# Revit family: IS_ConnectFreedom_E5485_BIM_DE
name_source: partatom
category: Plumbing Fixtures
revit_build: Autodesk Revit MEP 2015 (Build: 20140606_1530(x64)
units: mm (PartAtom-declared; Revit-internal decimal feet)

## types (1)
- E548501 - CONNECT FREEDOM - Basin 60X55 White
    BIMobject category = Basins
    BOSUseNativeGeometries = 1
    Brand url = http://www.idealstandard.co.uk
    Description = E548501 CONNECT FREEDOM accessible washbasin 600x555mm, 1 taphole, no overflow
    DrainSize = 42 mm  [stored 0.137795 ft]
    EAN code = https://5017830470328
    Edition number = 1
    IfcExportAs = WASHHANDBASIN
    IfcExportType = WASHBASIN
    Installation instructions = http://www.idealspec.co.uk
    Manufacturer name = Ideal Standard
    ManufacturerURL = www.idealstandard.com
    Material = Vitreous china
    Material main = Ceramics
    Model = E548501
    ModelNumber = E548501
    Name = CONNECT FREEDOM accessible washbasin 600x555mm, 1 taphole, no overflow
    NettWeight = 17.5 kg
    Nominal height = 165
    Nominal width = 600
    NominalDepth = 0 mm  [stored 0 ft]
    NominalHeight = 165 mm  [stored 0.541339 ft]
    NominalLength = 555 mm  [stored 1.82087 ft]
    NominalWidth = 600 mm  [stored 1.9685 ft]
    Product Guid = 22481b7c-1a44-404c-99cc-5ae21300aec6
    Product SKU = E5485
    Product data url = https://bimobject.com
    Product family = CONNECT FREEDOM
    Product group = Basin
    Product name = CONNECT FREEDOM - Basin 60X55 White
    Product url = http://www.idealspec.co.uk
    ProductInformation = www.idealstandard.de/produkte
    QR code = http://bimobject.com
    Shape = Sculptured
    Size = 600x555x165
    Space = Internal
    SpareParts = www.idealstandard.de/ersatzteile
    Technical description = http://www.idealspec.co.uk
    URL = www.idealstandard.com
    Uniclass 2015 Code = Pr_40_20_96
    Uniclass 2015 Name = Wash basins, sinks and troughs
    Uniclass2015Code = Pr_40_20_96
    Version = 1
    VolumeUnits = Litres
    WarrantyDurationUnit = year
    WashHandBasinType = Hand Rinse
    Weight Net (Kg) = 17.5

note: [stored X ft] marks values corroborated as IEEE doubles in the binary element streams (Revit-internal decimal feet)

## geometry (parser evidence)
native form markers: Blend x4, Sweep x1
no freeform markers — native parametric forms only
